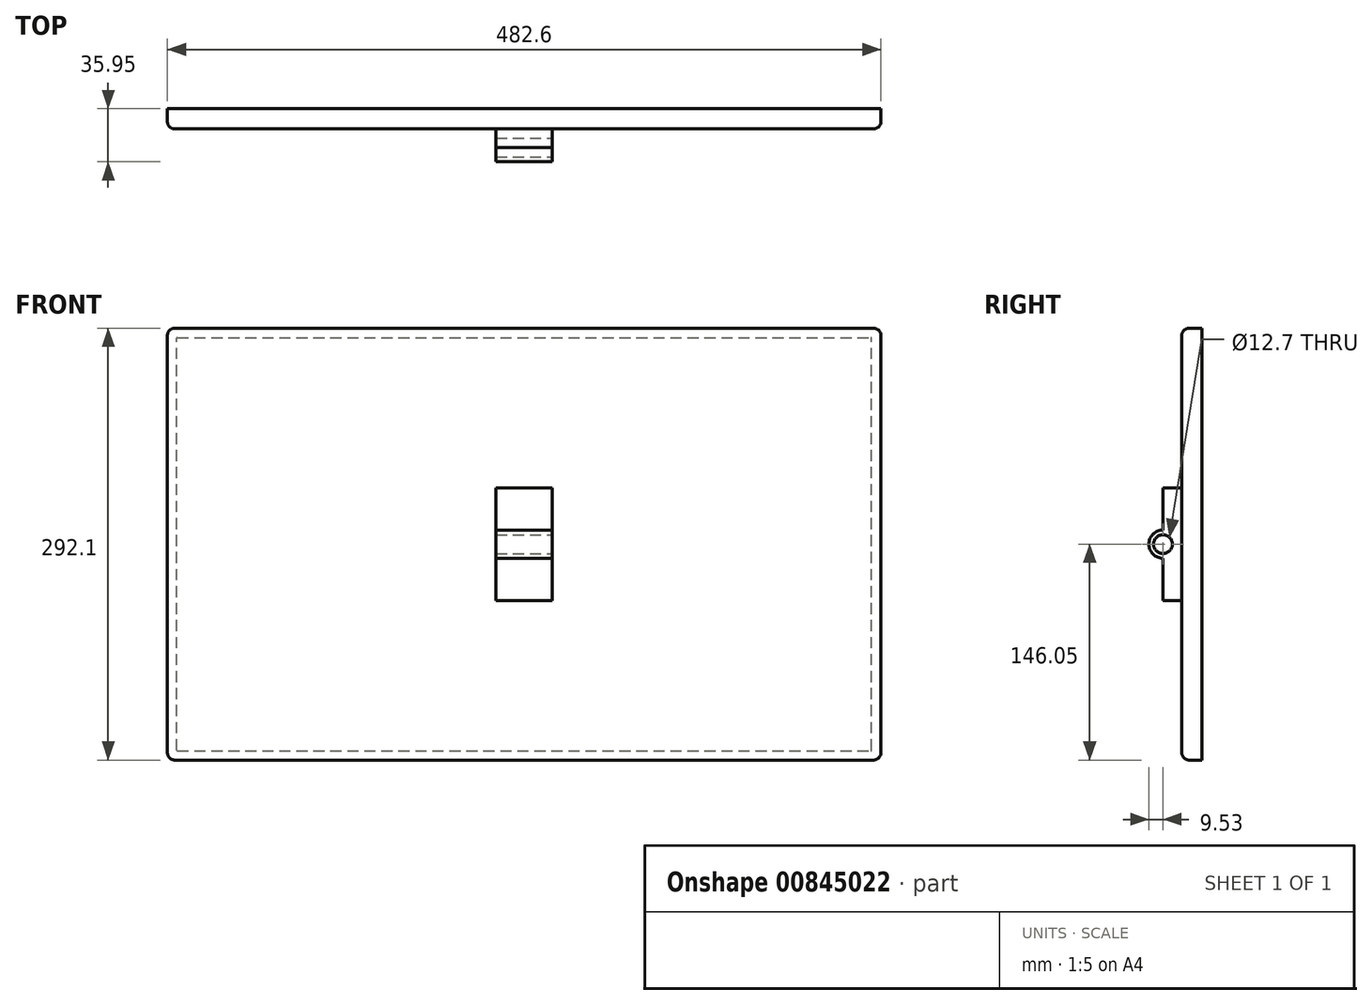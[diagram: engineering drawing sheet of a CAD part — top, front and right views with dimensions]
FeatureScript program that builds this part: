
annotation { "Feature Type Name" : "Feature", "Feature Type Description" : "" }
export const myFeature = defineFeature(function(context is Context, id is Id, definition is map)
    precondition{}
    {
        {
            var Q0;
            Q0=qCreatedBy(makeId("Front.planeOp"),FACE);
            var sketch = newSketch(context, id + "F0", { "sketchPlane" : qUnion([Q0])});
            skLineSegment(sketch, "E0.bottom", {"start": v(19.05, -38.1) * mm, "end": v(-19.05, -38.1) * mm});
            skLineSegment(sketch, "E0.top", {"start": v(19.05, 38.1) * mm, "end": v(-19.05, 38.1) * mm});
            skLineSegment(sketch, "E0.left", {"start": v(19.05, -38.1) * mm, "end": v(19.05, 38.1) * mm});
            skLineSegment(sketch, "E0.right", {"start": v(-19.05, -38.1) * mm, "end": v(-19.05, 38.1) * mm});
            skPoint(sketch, "E0.middle", {"position": v(0, 0) * mm});
            skSolve(sketch);
        }
        {
            var Q0;
            Q0=qSketchRegion(id+"F0",true);
            extrude(context, id + "F1", {"entities" : qUnion([Q0]), "depth" : 12.7 * mm, "offsetDistance" : 25.4 * mm});
        }
        {
            var Q0;
            Q0=makeQuery(id+"F1.opExtrude","SWEPT_FACE",FACE,{"disambiguationData":[OSD([sQuery(id+"F0.wireOp",EDGE,"E0.left")])]});
            var sketch = newSketch(context, id + "F2", { "sketchPlane" : qUnion([Q0])});
            skCircle(sketch, "E1", {"center": v(-12.7, 0) * mm, "radius": 9.53 * mm});
            skSolve(sketch);
        }
        {
            var Q0;
            Q0=qSketchRegion(id+"F2",true);
            extrude(context, id + "F3", {"entities" : qUnion([Q0]), "operationType" : NewBodyOperationType.ADD, "oppositeDirection" : true, "depth" : 38.1 * mm, "offsetDistance" : 25.4 * mm});
        }
        {
            var Q0;
            Q0=makeQuery(id+"F3.boolean.opBoolean","MERGE",FACE,{"derivedFrom":[makeQuery(id+"F1.opExtrude","SWEPT_FACE",FACE,{"disambiguationData":[OSD([sQuery(id+"F0.wireOp",EDGE,"E0.left")])]}),makeQuery(id+"F3.opExtrude","CAP_FACE",FACE,{"disambiguationData":[OSD([sQuery(id+"F2.wireOp",EDGE,"E1")])],"isStart":true})]});
            var sketch = newSketch(context, id + "F4", { "sketchPlane" : qUnion([Q0])});
            skCircle(sketch, "E2", {"center": v(-12.7, 0) * mm, "radius": 6.35 * mm});
            skSolve(sketch);
        }
        {
            var Q0;
            Q0=qSketchRegion(id+"F4",true);
            extrude(context, id + "F5", {"entities" : qUnion([Q0]), "operationType" : NewBodyOperationType.REMOVE, "oppositeDirection" : true, "depth" : 40.4 * mm, "offsetDistance" : 25.4 * mm});
        }
        {
            var Q0;
            Q0=makeQuery(id+"F1.opExtrude","CAP_FACE",FACE,{"disambiguationData":[OSD([sQuery(id+"F0.wireOp",EDGE,"E0.bottom"),sQuery(id+"F0.wireOp",EDGE,"E0.top"),sQuery(id+"F0.wireOp",EDGE,"E0.left"),sQuery(id+"F0.wireOp",EDGE,"E0.right")])],"isStart":true});
            var sketch = newSketch(context, id + "F6", { "sketchPlane" : qUnion([Q0])});
            skLineSegment(sketch, "E3.bottom", {"start": v(241.3, -146.05) * mm, "end": v(-241.3, -146.05) * mm});
            skLineSegment(sketch, "E3.top", {"start": v(241.3, 146.05) * mm, "end": v(-241.3, 146.05) * mm});
            skLineSegment(sketch, "E3.left", {"start": v(241.3, -146.05) * mm, "end": v(241.3, 146.05) * mm});
            skLineSegment(sketch, "E3.right", {"start": v(-241.3, -146.05) * mm, "end": v(-241.3, 146.05) * mm});
            skPoint(sketch, "E3.middle", {"position": v(0, 0) * mm});
            skSolve(sketch);
        }
        {
            var Q0;
            Q0 = qSketchRegion(id + "F6", true);
            extrude(context, id + "F7", {"entities" : qUnion([Q0]), "operationType" : NewBodyOperationType.ADD, "depth" : 13.72 * mm, "offsetDistance" : 25.4 * mm});
        }
        {
            var Q0;
            Q0=makeQuery(id+"F7.opExtrude","SWEPT_EDGE",EDGE,{"disambiguationData":[OSD([sQuery(id+"F6.wireOp",EDGE,"E3.top"),sQuery(id+"F6.wireOp",EDGE,"E3.left")])]});
            var Q1;
            Q1=makeQuery(id+"F7.opExtrude","SWEPT_EDGE",EDGE,{"disambiguationData":[OSD([sQuery(id+"F6.wireOp",EDGE,"E3.bottom"),sQuery(id+"F6.wireOp",EDGE,"E3.left")])]});
            var Q2;
            Q2=makeQuery(id+"F7.opExtrude","SWEPT_EDGE",EDGE,{"disambiguationData":[OSD([sQuery(id+"F6.wireOp",EDGE,"E3.bottom"),sQuery(id+"F6.wireOp",EDGE,"E3.right")])]});
            var Q3;
            Q3=makeQuery(id+"F7.opExtrude","SWEPT_EDGE",EDGE,{"disambiguationData":[OSD([sQuery(id+"F6.wireOp",EDGE,"E3.top"),sQuery(id+"F6.wireOp",EDGE,"E3.right")])]});
            var Q4;
            Q4=makeQuery(id+"F7.opExtrude","CAP_EDGE",EDGE,{"disambiguationData":[OSD([sQuery(id+"F6.wireOp",EDGE,"E3.right")])],"isStart":true});
            var Q5;
            Q5=makeQuery(id+"F7.opExtrude","CAP_EDGE",EDGE,{"disambiguationData":[OSD([sQuery(id+"F6.wireOp",EDGE,"E3.top")])],"isStart":true});
            var Q6;
            Q6=makeQuery(id+"F7.opExtrude","CAP_EDGE",EDGE,{"disambiguationData":[OSD([sQuery(id+"F6.wireOp",EDGE,"E3.left")])],"isStart":true});
            var Q7;
            Q7=makeQuery(id+"F7.opExtrude","CAP_EDGE",EDGE,{"disambiguationData":[OSD([sQuery(id+"F6.wireOp",EDGE,"E3.bottom")])],"isStart":true});
            fillet(context, id + "F8", {"entities" : qUnion([Q0, Q1, Q2, Q3, Q4, Q5, Q6, Q7]), "radius" : 5.08 * mm, "tangentPropagation" : true, "allowEdgeOverflow" : false});
        }
        {
            var Q0;
            Q0=makeQuery(id+"F7.opExtrude","CAP_FACE",FACE,{"disambiguationData":[OSD([sQuery(id+"F6.wireOp",EDGE,"E3.bottom"),sQuery(id+"F6.wireOp",EDGE,"E3.top"),sQuery(id+"F6.wireOp",EDGE,"E3.left"),sQuery(id+"F6.wireOp",EDGE,"E3.right")])],"isStart":false});
            var sketch = newSketch(context, id + "F9", { "sketchPlane" : qUnion([Q0])});
            skLineSegment(sketch, "E4.bottom", {"start": v(234.57, -139.7) * mm, "end": v(-234.57, -139.7) * mm});
            skLineSegment(sketch, "E4.top", {"start": v(234.57, 139.7) * mm, "end": v(-234.57, 139.7) * mm});
            skLineSegment(sketch, "E4.left", {"start": v(234.95, -139.32) * mm, "end": v(234.95, 139.32) * mm});
            skLineSegment(sketch, "E4.right", {"start": v(-234.95, -139.32) * mm, "end": v(-234.95, 139.32) * mm});
            skPoint(sketch, "E4.middle", {"position": v(0, 0) * mm});
            skPoint(sketch, "E5.visualSharp", {"position": v(-234.95, 139.7) * mm});
            skArc(sketch, "E5.filletArc", {"start": v(-234.57, 139.7) * mm, "mid": v(-234.84, 139.59) * mm, "end": v(-234.95, 139.32) * mm});
            skPoint(sketch, "E6.visualSharp", {"position": v(234.95, 139.7) * mm});
            skArc(sketch, "E6.filletArc", {"start": v(234.95, 139.32) * mm, "mid": v(234.84, 139.59) * mm, "end": v(234.57, 139.7) * mm});
            skPoint(sketch, "E7.visualSharp", {"position": v(234.95, -139.7) * mm});
            skArc(sketch, "E7.filletArc", {"start": v(234.57, -139.7) * mm, "mid": v(234.84, -139.59) * mm, "end": v(234.95, -139.32) * mm});
            skPoint(sketch, "E8.visualSharp", {"position": v(-234.95, -139.7) * mm});
            skArc(sketch, "E8.filletArc", {"start": v(-234.95, -139.32) * mm, "mid": v(-234.84, -139.59) * mm, "end": v(-234.57, -139.7) * mm});
            skSolve(sketch);
        }
        {
            var Q0;
            Q0 = qSketchRegion(id + "F9", true);
            extrude(context, id + "F10", {"entities" : qUnion([Q0]), "operationType" : NewBodyOperationType.REMOVE, "oppositeDirection" : true, "depth" : 0.25 * mm, "offsetDistance" : 25.4 * mm});
        }
    });
